# Revit family: T-956
name_source: partatom
category: Plumbing Fixtures
revit_build: Autodesk Revit Architecture 2012 (Build: 20110309_2315(x64)
units: mm (PartAtom-declared; Revit-internal decimal feet)

## types (1)
- T-956
    Assembly Code = D2010
    CW Connection = Yes
    CWFU = 0
    Cost = 0 $
    DEfault Elevation = 0' - 0"
    Description = Undertile mixer single lever. 2 X 1/2"FI, 1 X 1/2" + 1 X 3/4" female outlet
    HW Connection = Yes
    HWFU = 0
    Handle = S-T950-3CP
    Keynote = 2 x 1/2" female inlets, 1 x 1/2" shower outlet and 1 x 3/4" female bath outlet
    Manufacturer = COBRA
    Material = hrome - Polished
    Model = T-956
    Raised cartridge = S-SE950-1-R
    Range = Taryn Classic handle
    Type Comments = SANS 1480
    URL = http://www.cobra.co.za
    Undertile face plate = S-T950-5CP
    Vent Connection = No
    WFU = 0
    Waste Connection = No

## geometry (parser evidence)
native form markers: Blend x2
no freeform markers — native parametric forms only
